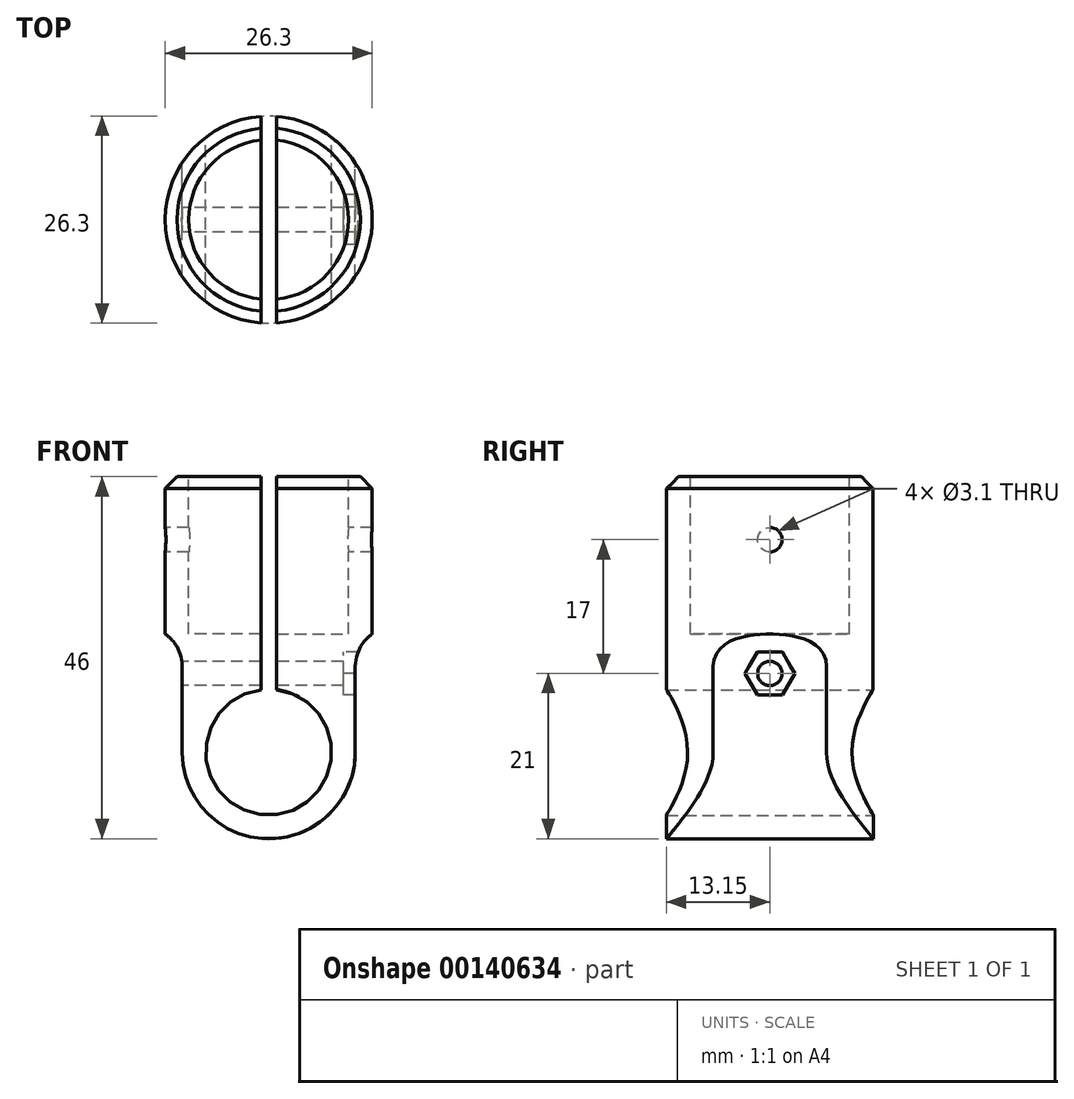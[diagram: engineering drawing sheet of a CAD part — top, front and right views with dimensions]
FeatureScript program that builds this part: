
annotation { "Feature Type Name" : "Feature", "Feature Type Description" : "" }
export const myFeature = defineFeature(function(context is Context, id is Id, definition is map)
    precondition{}
    {
        {
            var Q0;
            Q0=qCreatedBy(makeId("Top.planeOp"),FACE);
            var sketch = newSketch(context, id + "F0", { "sketchPlane" : qUnion([Q0])});
            skCircle(sketch, "E0", {"center": v(0, 0) * mm, "radius": 10.15 * mm});
            skCircle(sketch, "E1.0", {"center": v(0, 0) * mm, "radius": 13.15 * mm});
            skSolve(sketch);
        }
        {
            var Q0;
            Q0=makeQuery(id+"F0.imprint","IMPRINT",FACE,{"disambiguationData":[TD([[makeQuery(id+"F0.imprint","IMPRINT",EDGE,{"derivedFrom":sQuery(id+"F0.wireOp",EDGE,"E0")}),-1.0]])]});
            extrude(context, id + "F1", {"entities" : qUnion([Q0]), "oppositeDirection" : true, "depth" : 20 * mm});
        }
        {
            var Q0;
            Q0=qCreatedBy(makeId("Front.planeOp"),FACE);
            var sketch = newSketch(context, id + "F2", { "sketchPlane" : qUnion([Q0])});
            skCircle(sketch, "E2", {"center": v(0, -35) * mm, "radius": 8 * mm});
            skCircle(sketch, "E3.0", {"center": v(0, -35) * mm, "radius": 11 * mm});
            skLineSegment(sketch, "E4", {"start": v(0, -35) * mm, "end": v(-32.94, -35) * mm, "construction": true});
            skLineSegment(sketch, "E5", {"start": v(-11, -35) * mm, "end": v(-11, -24.08) * mm});
            skLineSegment(sketch, "E6.0", {"start": v(-13.15, -20) * mm, "end": v(13.15, -20) * mm});
            skArc(sketch, "E7", {"start": v(-11, -24.08) * mm, "mid": v(-11.57, -21.77) * mm, "end": v(-13.15, -20) * mm});
            skLineSegment(sketch, "E8", {"start": v(0, -35) * mm, "end": v(0, -18.04) * mm, "construction": true});
            skPoint(sketch, "E8.endSnap0", {"position": v(0, -20) * mm});
            skLineSegment(sketch, "E9.MirrorCS", {"start": v(11, -35) * mm, "end": v(11, -24.08) * mm});
            skArc(sketch, "E10.MirrorCS", {"start": v(11, -24.08) * mm, "mid": v(11.57, -21.77) * mm, "end": v(13.15, -20) * mm});
            skSolve(sketch);
        }
        {
            var Q0;
            Q0 = qSketchRegion(id + "F2", true);
            extrude(context, id + "F3", {"entities" : qUnion([Q0]), "operationType" : NewBodyOperationType.ADD, "endBound" : BoundingType.SYMMETRIC, "depth" : 45 * mm});
        }
        {
            var Q0;
            Q0=makeQuery(id+"F1.opExtrude","CAP_FACE",FACE,{"disambiguationData":[OSD([sQuery(id+"F0.wireOp",EDGE,"E0"),sQuery(id+"F0.wireOp",EDGE,"E1.0")])],"isStart":true});
            var sketch = newSketch(context, id + "F4", { "sketchPlane" : qUnion([Q0])});
            skCircle(sketch, "E11", {"center": v(0, 0) * mm, "radius": 40.4 * mm});
            skCircle(sketch, "E12.0", {"center": v(0, 0) * mm, "radius": 13.15 * mm});
            skSolve(sketch);
        }
        {
            var Q0;
            Q0=makeQuery(id+"F4.imprint","IMPRINT",FACE,{"disambiguationData":[TD([[makeQuery(id+"F4.imprint","IMPRINT",EDGE,{"derivedFrom":sQuery(id+"F4.wireOp",EDGE,"E11")}),1.0]])]});
            extrude(context, id + "F5", {"entities" : qUnion([Q0]), "operationType" : NewBodyOperationType.REMOVE, "oppositeDirection" : true, "depth" : 50 * mm});
        }
        {
            var Q0;
            Q0=makeQuery(id+"F1.opExtrude","CAP_FACE",FACE,{"disambiguationData":[OSD([sQuery(id+"F0.wireOp",EDGE,"E0"),sQuery(id+"F0.wireOp",EDGE,"E1.0")])],"isStart":true});
            var sketch = newSketch(context, id + "F6", { "sketchPlane" : qUnion([Q0])});
            skLineSegment(sketch, "E13.bottom", {"start": v(1, -17.5) * mm, "end": v(-1, -17.5) * mm});
            skLineSegment(sketch, "E13.top", {"start": v(1, 17.5) * mm, "end": v(-1, 17.5) * mm});
            skLineSegment(sketch, "E13.left", {"start": v(1, -17.5) * mm, "end": v(1, 17.5) * mm});
            skLineSegment(sketch, "E13.right", {"start": v(-1, -17.5) * mm, "end": v(-1, 17.5) * mm});
            skPoint(sketch, "E13.middle", {"position": v(0, 0) * mm});
            skSolve(sketch);
        }
        {
            var Q0;
            Q0 = qSketchRegion(id + "F6", true);
            extrude(context, id + "F7", {"entities" : qUnion([Q0]), "operationType" : NewBodyOperationType.REMOVE, "oppositeDirection" : true, "depth" : 31.26 * mm});
        }
        {
            var Q0;
            {var subQ0=sQuery(id+"F0.wireOp",EDGE,"E1.0");Q0=makeQuery(id+"F7.boolean.opBoolean","SPLIT",EDGE,{"disambiguationData":[TD([makeQuery(id+"F7.opExtrude","SWEPT_FACE",FACE,{"disambiguationData":[OSD([sQuery(id+"F6.wireOp",EDGE,"E13.right")])]})])],"derivedFrom":makeQuery(id+"F1.opExtrude","CAP_EDGE",EDGE,{"disambiguationData":[OSD([subQ0])],"isStart":true})});}
            var Q1;
            {var subQ0=sQuery(id+"F0.wireOp",EDGE,"E1.0");Q1=makeQuery(id+"F7.boolean.opBoolean","SPLIT",EDGE,{"disambiguationData":[TD([makeQuery(id+"F7.opExtrude","SWEPT_FACE",FACE,{"disambiguationData":[OSD([sQuery(id+"F6.wireOp",EDGE,"E13.left")])]})])],"derivedFrom":makeQuery(id+"F1.opExtrude","CAP_EDGE",EDGE,{"disambiguationData":[OSD([subQ0])],"isStart":true})});}
            chamfer(context, id + "F8", {"entities" : qUnion([Q0, Q1]), "width" : 1.5 * mm, "tangentPropagation" : true});
        }
        {
            var Q0;
            Q0=makeQuery(id+"F3.opExtrude","SWEPT_FACE",FACE,{"disambiguationData":[OSD([sQuery(id+"F2.wireOp",EDGE,"E5")])]});
            var sketch = newSketch(context, id + "F9", { "sketchPlane" : qUnion([Q0])});
            skCircle(sketch, "E14", {"center": v(0, -25) * mm, "radius": 1.55 * mm});
            skCircle(sketch, "E15", {"center": v(0, -8) * mm, "radius": 1.55 * mm});
            skSolve(sketch);
        }
        {
            var Q0;
            Q0 = qSketchRegion(id + "F9", true);
            extrude(context, id + "F10", {"entities" : qUnion([Q0]), "operationType" : NewBodyOperationType.REMOVE, "endBound" : BoundingType.SYMMETRIC, "oppositeDirection" : true, "depth" : 61.02 * mm});
        }
        {
            var Q0;
            Q0=makeQuery(id+"F3.opExtrude","SWEPT_FACE",FACE,{"disambiguationData":[OSD([sQuery(id+"F2.wireOp",EDGE,"E9.MirrorCS")])]});
            var sketch = newSketch(context, id + "F11", { "sketchPlane" : qUnion([Q0])});
            skCircle(sketch, "E16.cCircle", {"center": v(0, -25) * mm, "radius": 2.75 * mm, "construction": true});
            skLineSegment(sketch, "E16.0", {"start": v(-1.59, -22.25) * mm, "end": v(1.59, -22.25) * mm});
            skLineSegment(sketch, "E16.1", {"start": v(1.59, -22.25) * mm, "end": v(3.18, -25) * mm});
            skLineSegment(sketch, "E16.2", {"start": v(3.18, -25) * mm, "end": v(1.59, -27.75) * mm});
            skLineSegment(sketch, "E16.3", {"start": v(1.59, -27.75) * mm, "end": v(-1.59, -27.75) * mm});
            skLineSegment(sketch, "E16.4", {"start": v(-1.59, -27.75) * mm, "end": v(-3.18, -25) * mm});
            skLineSegment(sketch, "E16.5", {"start": v(-3.18, -25) * mm, "end": v(-1.59, -22.25) * mm});
            skPoint(sketch, "E16.0.midPoint", {"position": v(0, -22.25) * mm});
            skSolve(sketch);
        }
        {
            var Q0;
            Q0 = qSketchRegion(id + "F11", true);
            extrude(context, id + "F12", {"entities" : qUnion([Q0]), "operationType" : NewBodyOperationType.REMOVE, "endBound" : BoundingType.SYMMETRIC, "depth" : 3 * mm});
        }
    });
